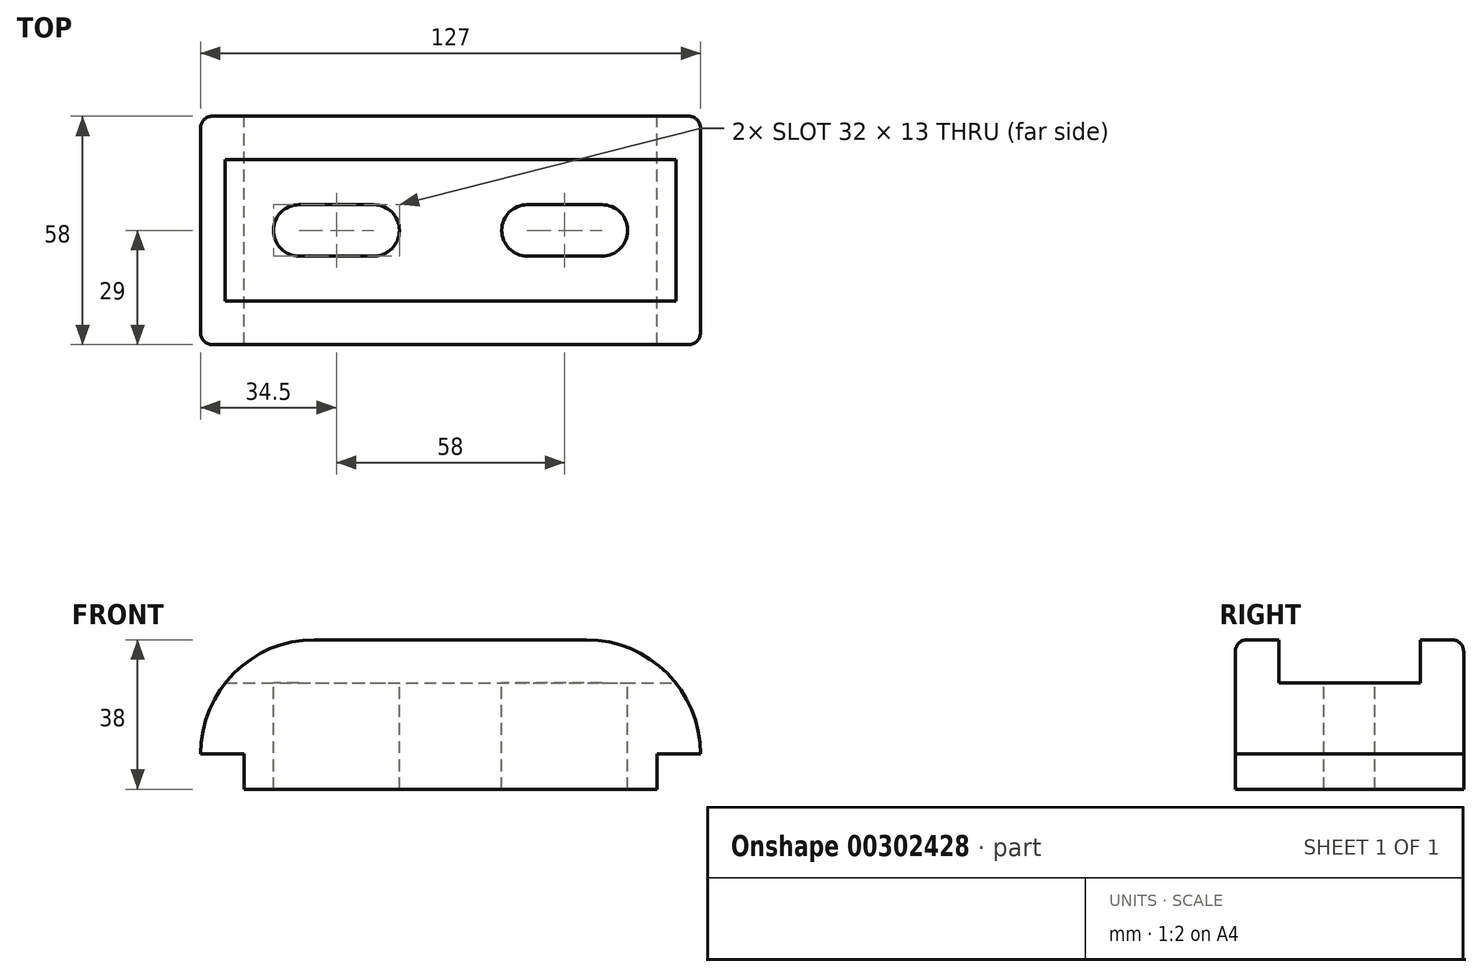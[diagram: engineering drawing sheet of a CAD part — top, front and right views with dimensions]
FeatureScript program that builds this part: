
annotation { "Feature Type Name" : "Feature", "Feature Type Description" : "" }
export const myFeature = defineFeature(function(context is Context, id is Id, definition is map)
    precondition{}
    {
        {
            var Q0;
            Q0=qCreatedBy(makeId("Front.planeOp"),FACE);
            var sketch = newSketch(context, id + "F0", { "sketchPlane" : qUnion([Q0])});
            skLineSegment(sketch, "E0", {"start": v(-52.5, 0) * mm, "end": v(52.5, 0) * mm});
            skLineSegment(sketch, "E1", {"start": v(52.5, 0) * mm, "end": v(52.5, 9) * mm});
            skLineSegment(sketch, "E2", {"start": v(52.5, 9) * mm, "end": v(63.5, 9) * mm});
            skLineSegment(sketch, "E3", {"start": v(-52.5, 0) * mm, "end": v(-52.5, 9) * mm});
            skLineSegment(sketch, "E4", {"start": v(-52.5, 9) * mm, "end": v(-63.5, 9) * mm});
            skLineSegment(sketch, "E5", {"start": v(-34.5, 38) * mm, "end": v(34.5, 38) * mm});
            skPoint(sketch, "E6.visualSharp", {"position": v(-48.92, 38) * mm});
            skArc(sketch, "E6.filletArc", {"start": v(-34.5, 38) * mm, "mid": v(-55, 29.5) * mm, "end": v(-63.5, 9) * mm});
            skPoint(sketch, "E7.visualSharp", {"position": v(63.5, 38) * mm});
            skArc(sketch, "E7.filletArc", {"start": v(63.5, 9) * mm, "mid": v(55, 29.5) * mm, "end": v(34.5, 38) * mm});
            skSolve(sketch);
        }
        {
            var Q0;
            Q0=makeQuery(id+"F0.imprint","IMPRINT",FACE,{"disambiguationData":[TD([[makeQuery(id+"F0.imprint","IMPRINT",EDGE,{"derivedFrom":sQuery(id+"F0.wireOp",EDGE,"E0")}),1.0]])]});
            extrude(context, id + "F1", {"entities" : qUnion([Q0]), "depth" : 58 * mm});
        }
        {
            var Q0;
            Q0=qCreatedBy(makeId("Right.planeOp"),FACE);
            cPlane(context, id + "F2", {"entities" : qUnion([Q0]), "cplaneType" : CPlaneType.OFFSET, "offset" : 75 * mm, "width" : 150 * mm, "height" : 150 * mm});
        }
        {
            var Q0;
            Q0=qCreatedBy(id+"F2.planeOp",FACE);
            var sketch = newSketch(context, id + "F3", { "sketchPlane" : qUnion([Q0])});
            skLineSegment(sketch, "E8.bottom", {"start": v(-47, 38) * mm, "end": v(-11, 38) * mm});
            skLineSegment(sketch, "E8.top", {"start": v(-47, 27) * mm, "end": v(-11, 27) * mm});
            skLineSegment(sketch, "E8.left", {"start": v(-47, 38) * mm, "end": v(-47, 27) * mm});
            skLineSegment(sketch, "E8.right", {"start": v(-11, 38) * mm, "end": v(-11, 27) * mm});
            skSolve(sketch);
        }
        {
            var Q0;
            Q0 = qSketchRegion(id + "F3", true);
            extrude(context, id + "F4", {"entities" : qUnion([Q0]), "operationType" : NewBodyOperationType.REMOVE, "endBound" : BoundingType.THROUGH_ALL, "oppositeDirection" : true, "depth" : 25 * mm});
        }
        {
            var Q0;
            Q0=makeQuery(id+"F4.boolean.opBoolean","COPY",FACE,{"derivedFrom":makeQuery(id+"F4.opExtrude","SWEPT_FACE",FACE,{"disambiguationData":[OSD([sQuery(id+"F3.wireOp",EDGE,"E8.top")])]})});
            var sketch = newSketch(context, id + "F5", { "sketchPlane" : qUnion([Q0])});
            skLineSegment(sketch, "E9", {"start": v(0, 0) * mm, "end": v(0, -58) * mm, "construction": true});
            skPoint(sketch, "E9.endSnap0", {"position": v(0, -47) * mm});
            skArc(sketch, "E10", {"start": v(-38.5, -22.5) * mm, "mid": v(-45, -29) * mm, "end": v(-38.5, -35.5) * mm});
            skPoint(sketch, "E10.centerSnap0", {"position": v(0, -29) * mm});
            skArc(sketch, "E11", {"start": v(-19.5, -35.5) * mm, "mid": v(-13, -29) * mm, "end": v(-19.5, -22.5) * mm});
            skLineSegment(sketch, "E12", {"start": v(-38.5, -22.5) * mm, "end": v(-19.5, -22.5) * mm});
            skLineSegment(sketch, "E13", {"start": v(-38.5, -35.5) * mm, "end": v(-19.5, -35.5) * mm});
            skLineSegment(sketch, "E14.MirrorCS", {"start": v(38.5, -22.5) * mm, "end": v(19.5, -22.5) * mm});
            skArc(sketch, "E15.MirrorCS", {"start": v(38.5, -22.5) * mm, "mid": v(45, -29) * mm, "end": v(38.5, -35.5) * mm});
            skLineSegment(sketch, "E16.MirrorCS", {"start": v(38.5, -35.5) * mm, "end": v(19.5, -35.5) * mm});
            skArc(sketch, "E17.MirrorCS", {"start": v(19.5, -35.5) * mm, "mid": v(13, -29) * mm, "end": v(19.5, -22.5) * mm});
            skLineSegment(sketch, "E18", {"start": v(-57.24, -29) * mm, "end": v(63.72, -29) * mm, "construction": true});
            skSolve(sketch);
        }
        {
            var Q0;
            Q0=makeQuery(id+"F5.imprint","IMPRINT",FACE,{"disambiguationData":[TD([[makeQuery(id+"F5.imprint","IMPRINT",EDGE,{"derivedFrom":sQuery(id+"F5.wireOp",EDGE,"E10")}),1.0]])]});
            var Q1;
            Q1=makeQuery(id+"F5.imprint","IMPRINT",FACE,{"disambiguationData":[TD([[makeQuery(id+"F5.imprint","IMPRINT",EDGE,{"derivedFrom":sQuery(id+"F5.wireOp",EDGE,"E14.MirrorCS")}),1.0]])]});
            extrude(context, id + "F6", {"entities" : qUnion([Q0, Q1]), "operationType" : NewBodyOperationType.REMOVE, "endBound" : BoundingType.THROUGH_ALL, "oppositeDirection" : true, "depth" : 25 * mm});
        }
        {
            var Q0;
            Q0=makeQuery(id+"F1.opExtrude","CAP_EDGE",EDGE,{"disambiguationData":[OSD([sQuery(id+"F0.wireOp",EDGE,"E5")])],"isStart":false});
            var Q1;
            Q1=makeQuery(id+"F1.opExtrude","CAP_EDGE",EDGE,{"disambiguationData":[OSD([sQuery(id+"F0.wireOp",EDGE,"E5")])],"isStart":true});
            fillet(context, id + "F7", {"entities" : qUnion([Q0, Q1]), "radius" : 3 * mm, "tangentPropagation" : true, "allowEdgeOverflow" : false});
        }
    });
